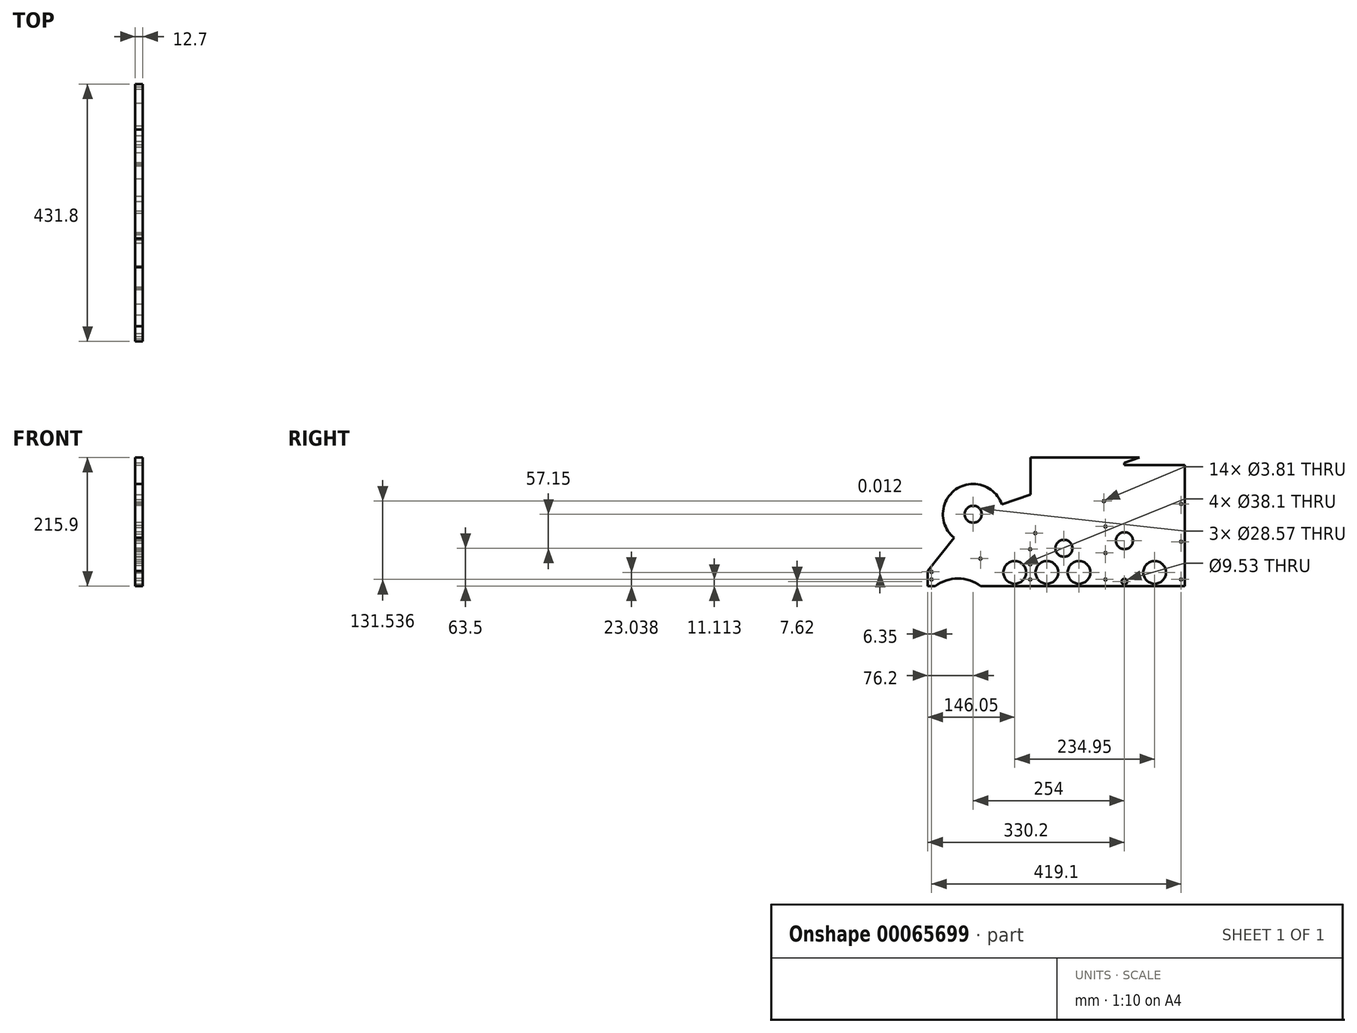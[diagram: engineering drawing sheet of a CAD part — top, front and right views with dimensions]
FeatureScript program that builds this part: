
annotation { "Feature Type Name" : "Feature", "Feature Type Description" : "" }
export const myFeature = defineFeature(function(context is Context, id is Id, definition is map)
    precondition{}
    {
        {
            var Q0;
            Q0=qCreatedBy(makeId("Right.planeOp"),FACE);
            var sketch = newSketch(context, id + "F0", { "sketchPlane" : qUnion([Q0])});
            skLineSegment(sketch, "E0.bottom", {"start": v(0, 0) * mm, "end": v(431.8, 0) * mm});
            skLineSegment(sketch, "E0.top", {"start": v(0, 355.6) * mm, "end": v(431.8, 355.6) * mm});
            skLineSegment(sketch, "E0.left", {"start": v(0, 0) * mm, "end": v(0, 355.6) * mm});
            skLineSegment(sketch, "E0.right", {"start": v(431.8, 0) * mm, "end": v(431.8, 355.6) * mm});
            skCircle(sketch, "E1", {"center": v(330.2, 7.62) * mm, "radius": 4.76 * mm});
            skCircle(sketch, "E2", {"center": v(228.6, 63.5) * mm, "radius": 14.29 * mm});
            skCircle(sketch, "E3", {"center": v(76.2, 120.65) * mm, "radius": 14.29 * mm});
            skCircle(sketch, "E4", {"center": v(330.2, 76.2) * mm, "radius": 14.29 * mm});
            skLineSegment(sketch, "E5", {"start": v(53.96, 29.94) * mm, "end": v(330.2, 158.75) * mm, "construction": true});
            skLineSegment(sketch, "E6", {"start": v(330.2, 158.75) * mm, "end": v(330.2, 29.94) * mm, "construction": true});
            skLineSegment(sketch, "E7", {"start": v(330.2, 29.94) * mm, "end": v(53.96, 29.94) * mm, "construction": true});
            skCircle(sketch, "E8", {"center": v(295.67, 142.65) * mm, "radius": 1.9 * mm});
            skCircle(sketch, "E9", {"center": v(88.49, 46.04) * mm, "radius": 1.9 * mm});
            skCircle(sketch, "E10", {"center": v(50.8, -50.8) * mm, "radius": 63.5 * mm});
            skCircle(sketch, "E11", {"center": v(180.57, 88.98) * mm, "radius": 1.9 * mm});
            skSolve(sketch);
        }
        {
            var Q0;
            Q0=makeQuery(id+"F0.imprint","IMPRINT",FACE,{"disambiguationData":[TD([[makeQuery(id+"F0.imprint","IMPRINT",EDGE,{"derivedFrom":sQuery(id+"F0.wireOp",EDGE,"E0.top")}),-1.0]])]});
            extrude(context, id + "F1", {"entities" : qUnion([Q0]), "depth" : 12.7 * mm});
        }
        {
            var Q0;
            Q0=makeQuery(id+"F1.opExtrude","CAP_FACE",FACE,{"disambiguationData":[OSD([sQuery(id+"F0.wireOp",EDGE,"E0.bottom"),sQuery(id+"F0.wireOp",EDGE,"E0.top"),sQuery(id+"F0.wireOp",EDGE,"E0.left"),sQuery(id+"F0.wireOp",EDGE,"E0.right"),sQuery(id+"F0.wireOp",EDGE,"E1"),sQuery(id+"F0.wireOp",EDGE,"E2"),sQuery(id+"F0.wireOp",EDGE,"E3"),sQuery(id+"F0.wireOp",EDGE,"E4"),sQuery(id+"F0.wireOp",EDGE,"E8"),sQuery(id+"F0.wireOp",EDGE,"E9"),sQuery(id+"F0.wireOp",EDGE,"E10")])],"isStart":false});
            var sketch = newSketch(context, id + "F2", { "sketchPlane" : qUnion([Q0])});
            skCircle(sketch, "E12", {"center": v(146.05, 23.05) * mm, "radius": 19.05 * mm});
            skCircle(sketch, "E13", {"center": v(254, 23.05) * mm, "radius": 19.05 * mm});
            skCircle(sketch, "E14", {"center": v(381, 23.04) * mm, "radius": 19.05 * mm});
            skCircle(sketch, "E15", {"center": v(200.03, 23.05) * mm, "radius": 19.05 * mm});
            skLineSegment(sketch, "E16", {"start": v(254, 23.05) * mm, "end": v(200.03, 23.05) * mm, "construction": true});
            skLineSegment(sketch, "E17", {"start": v(200.03, 23.05) * mm, "end": v(146.05, 23.05) * mm, "construction": true});
            skSolve(sketch);
        }
        {
            var Q0;
            Q0=qSketchRegion(id+"F2",true);
            extrude(context, id + "F3", {"entities" : qUnion([Q0]), "operationType" : NewBodyOperationType.REMOVE, "endBound" : BoundingType.UP_TO_NEXT, "oppositeDirection" : true, "depth" : 25.4 * mm});
        }
        {
            var Q0;
            Q0=makeQuery(id+"F1.opExtrude","CAP_FACE",FACE,{"disambiguationData":[OSD([sQuery(id+"F0.wireOp",EDGE,"E0.bottom"),sQuery(id+"F0.wireOp",EDGE,"E0.top"),sQuery(id+"F0.wireOp",EDGE,"E0.left"),sQuery(id+"F0.wireOp",EDGE,"E0.right"),sQuery(id+"F0.wireOp",EDGE,"E1"),sQuery(id+"F0.wireOp",EDGE,"E2"),sQuery(id+"F0.wireOp",EDGE,"E3"),sQuery(id+"F0.wireOp",EDGE,"E4"),sQuery(id+"F0.wireOp",EDGE,"E8"),sQuery(id+"F0.wireOp",EDGE,"E9"),sQuery(id+"F0.wireOp",EDGE,"E10")])],"isStart":false});
            var sketch = newSketch(context, id + "F4", { "sketchPlane" : qUnion([Q0])});
            skLineSegment(sketch, "E18.bottom", {"start": v(0, 355.6) * mm, "end": v(431.8, 355.6) * mm});
            skLineSegment(sketch, "E18.top", {"start": v(0, 215.9) * mm, "end": v(431.8, 215.9) * mm});
            skLineSegment(sketch, "E18.left", {"start": v(0, 355.6) * mm, "end": v(0, 215.9) * mm});
            skLineSegment(sketch, "E18.right", {"start": v(431.8, 355.6) * mm, "end": v(431.8, 215.9) * mm});
            skCircle(sketch, "E19", {"center": v(76.2, 120.65) * mm, "radius": 50.8 * mm});
            skLineSegment(sketch, "E20", {"start": v(76.2, 120.65) * mm, "end": v(355.6, 215.9) * mm});
            skLineSegment(sketch, "E21", {"start": v(76.2, 120.65) * mm, "end": v(0, 25.4) * mm});
            skLineSegment(sketch, "E22", {"start": v(172.37, 153.43) * mm, "end": v(172.37, 215.9) * mm});
            skLineSegment(sketch, "E23.bottom", {"start": v(431.8, 215.9) * mm, "end": v(330.2, 215.9) * mm});
            skLineSegment(sketch, "E23.top", {"start": v(431.8, 203.2) * mm, "end": v(330.2, 203.2) * mm});
            skLineSegment(sketch, "E23.left", {"start": v(431.8, 215.9) * mm, "end": v(431.8, 203.2) * mm});
            skLineSegment(sketch, "E23.right", {"start": v(330.2, 215.9) * mm, "end": v(330.2, 203.2) * mm});
            skSolve(sketch);
        }
        {
            var Q0;
            Q0=makeQuery(id+"F4.imprint","IMPRINT",FACE,{"disambiguationData":[TD([[makeQuery(id+"F4.imprint","IMPRINT",EDGE,{"derivedFrom":sQuery(id+"F4.wireOp",EDGE,"E18.bottom")}),-1.0]])]});
            var Q1;
            {var subQ0=sQuery(id+"F4.wireOp",EDGE,"E21");var subQ3=sQuery(id+"F4.wireOp",EDGE,"E19");var subQ4=makeQuery(id+"F4.imprint","INTERSECT",VERTEX,{"derivedFrom":[subQ3,subQ0]});Q1=makeQuery(id+"F4.imprint","IMPRINT",FACE,{"disambiguationData":[TD([[makeQuery(id+"F4.imprint","IMPRINT",EDGE,{"disambiguationData":[TD([[subQ4,1.0]])],"derivedFrom":subQ3}),-1.0]])]});}
            var Q2;
            Q2=makeQuery(id+"F4.imprint","IMPRINT",FACE,{"disambiguationData":[TD([[makeQuery(id+"F4.imprint","IMPRINT",EDGE,{"derivedFrom":sQuery(id+"F4.wireOp",EDGE,"E23.bottom")}),1.0]])]});
            var Q3;
            {var subQ1=sQuery(id+"F4.wireOp",EDGE,"E23.top");Q3=makeQuery(id+"F4.imprint","IMPRINT",FACE,{"disambiguationData":[TD([[makeQuery(id+"F4.imprint","IMPRINT",EDGE,{"derivedFrom":subQ1}),-1.0]])]});}
            extrude(context, id + "F5", {"entities" : qUnion([Q0, Q1, Q2, Q3]), "operationType" : NewBodyOperationType.REMOVE, "endBound" : BoundingType.UP_TO_NEXT, "oppositeDirection" : true, "depth" : 25.4 * mm});
        }
        {
            var Q0;
            Q0=makeQuery(id+"F1.opExtrude","CAP_FACE",FACE,{"disambiguationData":[OSD([sQuery(id+"F0.wireOp",EDGE,"E0.bottom"),sQuery(id+"F0.wireOp",EDGE,"E0.top"),sQuery(id+"F0.wireOp",EDGE,"E0.left"),sQuery(id+"F0.wireOp",EDGE,"E0.right"),sQuery(id+"F0.wireOp",EDGE,"E1"),sQuery(id+"F0.wireOp",EDGE,"E2"),sQuery(id+"F0.wireOp",EDGE,"E3"),sQuery(id+"F0.wireOp",EDGE,"E4"),sQuery(id+"F0.wireOp",EDGE,"E8"),sQuery(id+"F0.wireOp",EDGE,"E9"),sQuery(id+"F0.wireOp",EDGE,"E10"),sQuery(id+"F0.wireOp",EDGE,"E11")])],"isStart":false});
            var sketch = newSketch(context, id + "F6", { "sketchPlane" : qUnion([Q0])});
            skCircle(sketch, "E24", {"center": v(425.45, 11.11) * mm, "radius": 1.9 * mm});
            skCircle(sketch, "E25", {"center": v(425.45, 74.51) * mm, "radius": 1.9 * mm});
            skCircle(sketch, "E26", {"center": v(425.45, 137.9) * mm, "radius": 1.9 * mm});
            skCircle(sketch, "E27", {"center": v(298.45, 11.11) * mm, "radius": 1.9 * mm});
            skCircle(sketch, "E28", {"center": v(298.45, 100.01) * mm, "radius": 1.9 * mm});
            skCircle(sketch, "E29", {"center": v(298.45, 55.56) * mm, "radius": 1.9 * mm});
            skLineSegment(sketch, "E30", {"start": v(298.45, 11.11) * mm, "end": v(298.45, 55.56) * mm, "construction": true});
            skLineSegment(sketch, "E31", {"start": v(298.45, 100.01) * mm, "end": v(298.45, 55.56) * mm, "construction": true});
            skCircle(sketch, "E32", {"center": v(171.86, 11.11) * mm, "radius": 1.9 * mm});
            skCircle(sketch, "E33", {"center": v(171.86, 36.51) * mm, "radius": 1.9 * mm});
            skCircle(sketch, "E34", {"center": v(171.86, 61.91) * mm, "radius": 1.9 * mm});
            skLineSegment(sketch, "E35", {"start": v(171.86, 61.91) * mm, "end": v(171.86, 36.51) * mm, "construction": true});
            skLineSegment(sketch, "E36", {"start": v(171.86, 11.11) * mm, "end": v(171.86, 36.51) * mm, "construction": true});
            skCircle(sketch, "E37", {"center": v(6.35, 11.11) * mm, "radius": 1.9 * mm});
            skCircle(sketch, "E38", {"center": v(6.35, 23.81) * mm, "radius": 1.9 * mm});
            skSolve(sketch);
        }
        {
            var Q0;
            Q0=qSketchRegion(id+"F6",true);
            extrude(context, id + "F7", {"entities" : qUnion([Q0]), "operationType" : NewBodyOperationType.REMOVE, "endBound" : BoundingType.UP_TO_NEXT, "oppositeDirection" : true, "depth" : 25.4 * mm});
        }
    });
